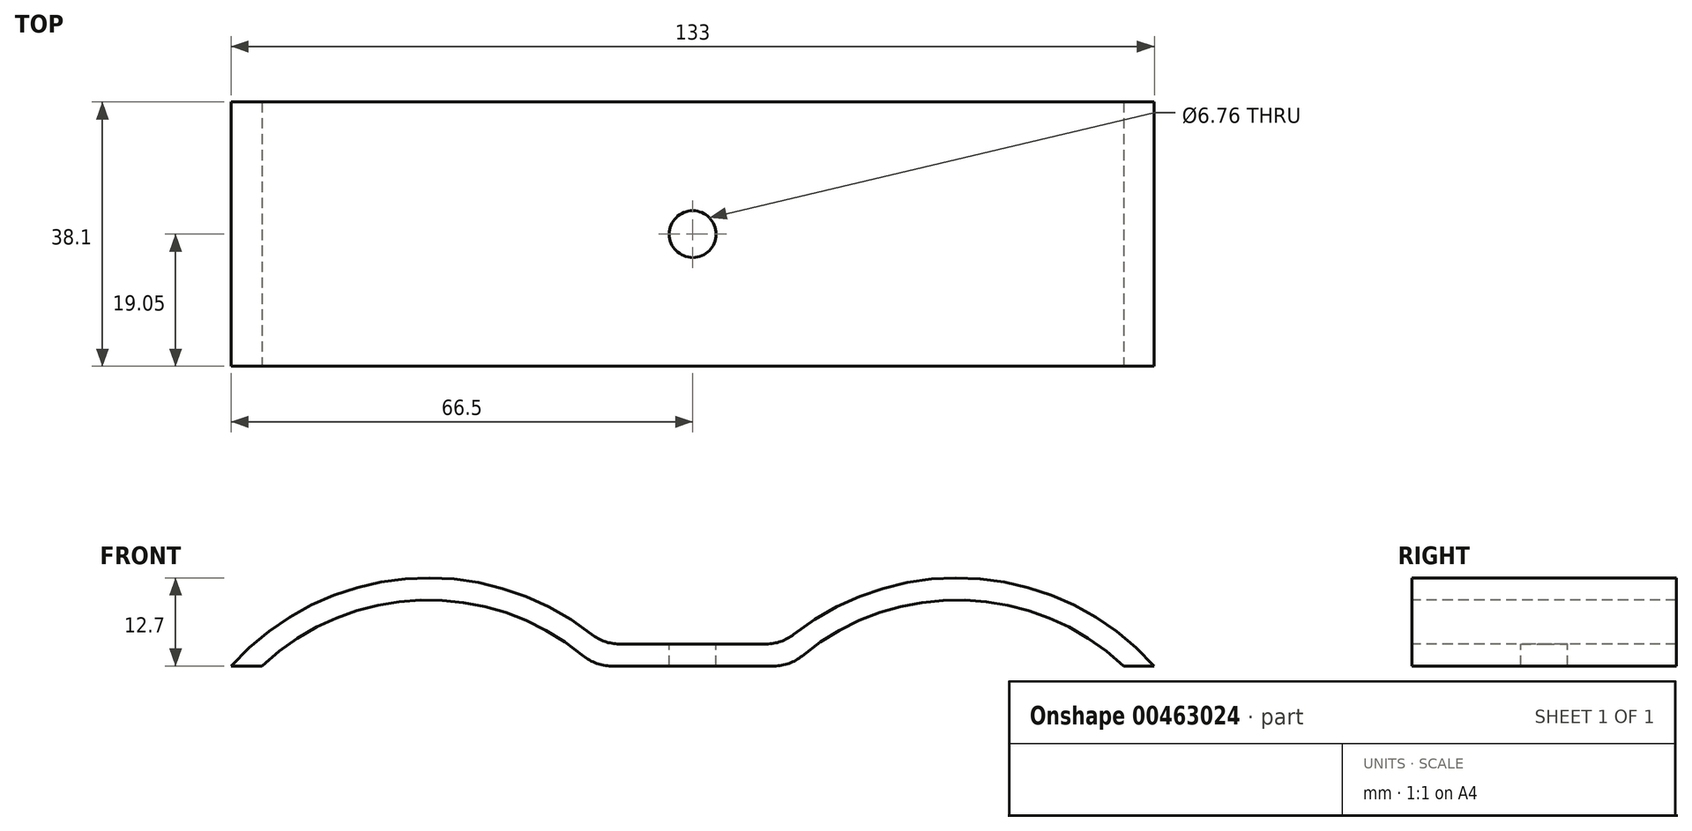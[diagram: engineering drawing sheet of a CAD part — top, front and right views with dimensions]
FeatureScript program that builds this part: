
annotation { "Feature Type Name" : "Feature", "Feature Type Description" : "" }
export const myFeature = defineFeature(function(context is Context, id is Id, definition is map)
    precondition{}
    {
        {
            var Q0;
            Q0=qCreatedBy(makeId("Front.planeOp"),FACE);
            var sketch = newSketch(context, id + "F0", { "sketchPlane" : qUnion([Q0])});
            skArc(sketch, "E0", {"start": v(-14.53, 4.54) * mm, "mid": v(-41.41, 12.56) * mm, "end": v(-66.5, 0) * mm});
            skArc(sketch, "E1.MirrorC", {"start": v(14.53, 4.54) * mm, "mid": v(41.41, 12.56) * mm, "end": v(66.5, 0) * mm});
            skLineSegment(sketch, "E2", {"start": v(-10.6, 3.18) * mm, "end": v(10.6, 3.18) * mm});
            skArc(sketch, "E3.0", {"start": v(15.78, 1.47) * mm, "mid": v(39.2, 9.5) * mm, "end": v(62.07, 0) * mm});
            skArc(sketch, "E4.0", {"start": v(-15.78, 1.47) * mm, "mid": v(-39.2, 9.5) * mm, "end": v(-62.07, 0) * mm});
            skLineSegment(sketch, "E5", {"start": v(-66.5, 0) * mm, "end": v(-62.07, 0) * mm});
            skLineSegment(sketch, "E6.trimOffspring", {"start": v(62.07, 0) * mm, "end": v(66.5, 0) * mm});
            skLineSegment(sketch, "E7.trimOffspring", {"start": v(-11.73, 0) * mm, "end": v(11.73, 0) * mm});
            skPoint(sketch, "E8.visualSharp", {"position": v(-12.9, 3.18) * mm});
            skArc(sketch, "E8.filletArc", {"start": v(-14.53, 4.54) * mm, "mid": v(-12.68, 3.52) * mm, "end": v(-10.6, 3.18) * mm});
            skPoint(sketch, "E9.visualSharp", {"position": v(12.9, 3.18) * mm});
            skArc(sketch, "E9.filletArc", {"start": v(10.6, 3.18) * mm, "mid": v(12.68, 3.52) * mm, "end": v(14.53, 4.54) * mm});
            skPoint(sketch, "E10.visualSharp", {"position": v(-14.13, 0) * mm});
            skArc(sketch, "E10.filletArc", {"start": v(-15.78, 1.47) * mm, "mid": v(-13.88, 0.38) * mm, "end": v(-11.73, 0) * mm});
            skPoint(sketch, "E11.visualSharp", {"position": v(14.13, 0) * mm});
            skArc(sketch, "E11.filletArc", {"start": v(11.73, 0) * mm, "mid": v(13.88, 0.38) * mm, "end": v(15.78, 1.47) * mm});
            skSolve(sketch);
        }
        {
            var Q0;
            Q0=makeQuery(id+"F0.imprint","IMPRINT",FACE,{"disambiguationData":[TD([[makeQuery(id+"F0.imprint","IMPRINT",EDGE,{"derivedFrom":sQuery(id+"F0.wireOp",EDGE,"E0")}),1.0]])]});
            extrude(context, id + "F1", {"entities" : qUnion([Q0]), "endBound" : BoundingType.SYMMETRIC, "oppositeDirection" : true, "depth" : 38.1 * mm});
        }
        {
            var Q0;
            Q0=makeQuery(id+"F1.opExtrude","SWEPT_FACE",FACE,{"disambiguationData":[OSD([sQuery(id+"F0.wireOp",EDGE,"E2")])]});
            var sketch = newSketch(context, id + "F2", { "sketchPlane" : qUnion([Q0])});
            skPoint(sketch, "E12", {"position": v(0, 0) * mm});
            skSolve(sketch);
        }
        {
            var Q0;
            Q0=sQuery(id+"F2.wireOp",VERTEX,"E12");
            var Q1;
            Q1=makeQuery(id+"F1.opExtrude","SWEPT_BODY",BODY,{"disambiguationData":[OSD([sQuery(id+"F0.wireOp",EDGE,"E0"),sQuery(id+"F0.wireOp",EDGE,"E1.MirrorC"),sQuery(id+"F0.wireOp",EDGE,"E2"),sQuery(id+"F0.wireOp",EDGE,"E3.0"),sQuery(id+"F0.wireOp",EDGE,"E4.0"),sQuery(id+"F0.wireOp",EDGE,"E5"),sQuery(id+"F0.wireOp",EDGE,"E6.trimOffspring"),sQuery(id+"F0.wireOp",EDGE,"E7.trimOffspring"),sQuery(id+"F0.wireOp",EDGE,"E8.filletArc"),sQuery(id+"F0.wireOp",EDGE,"E9.filletArc"),sQuery(id+"F0.wireOp",EDGE,"E10.filletArc"),sQuery(id+"F0.wireOp",EDGE,"E11.filletArc")])]});
            hole(context, id + "F3", {"style" : HoleStyle.SIMPLE, "endStyle" : HoleEndStyle.THROUGH, "standardTappedOrClearance" : lookupTablePath({ "standard" : "ANSI", "fit" : "Normal (ASME)", "size" : "1/4", "type" : "Clearance" }), "standardBlindInLast" : lookupTablePath({ "fit" : "Free", "standard" : "ANSI", "size" : "1/4", "type" : "Clearance" }), "holeDiameter" : 6.76 * mm, "isTappedThrough" : true, "tappedDepth" : 12.7 * mm, "tapClearance" : 3, "locations" : qUnion([Q0]), "scope" : qUnion([Q1])});
        }
    });
